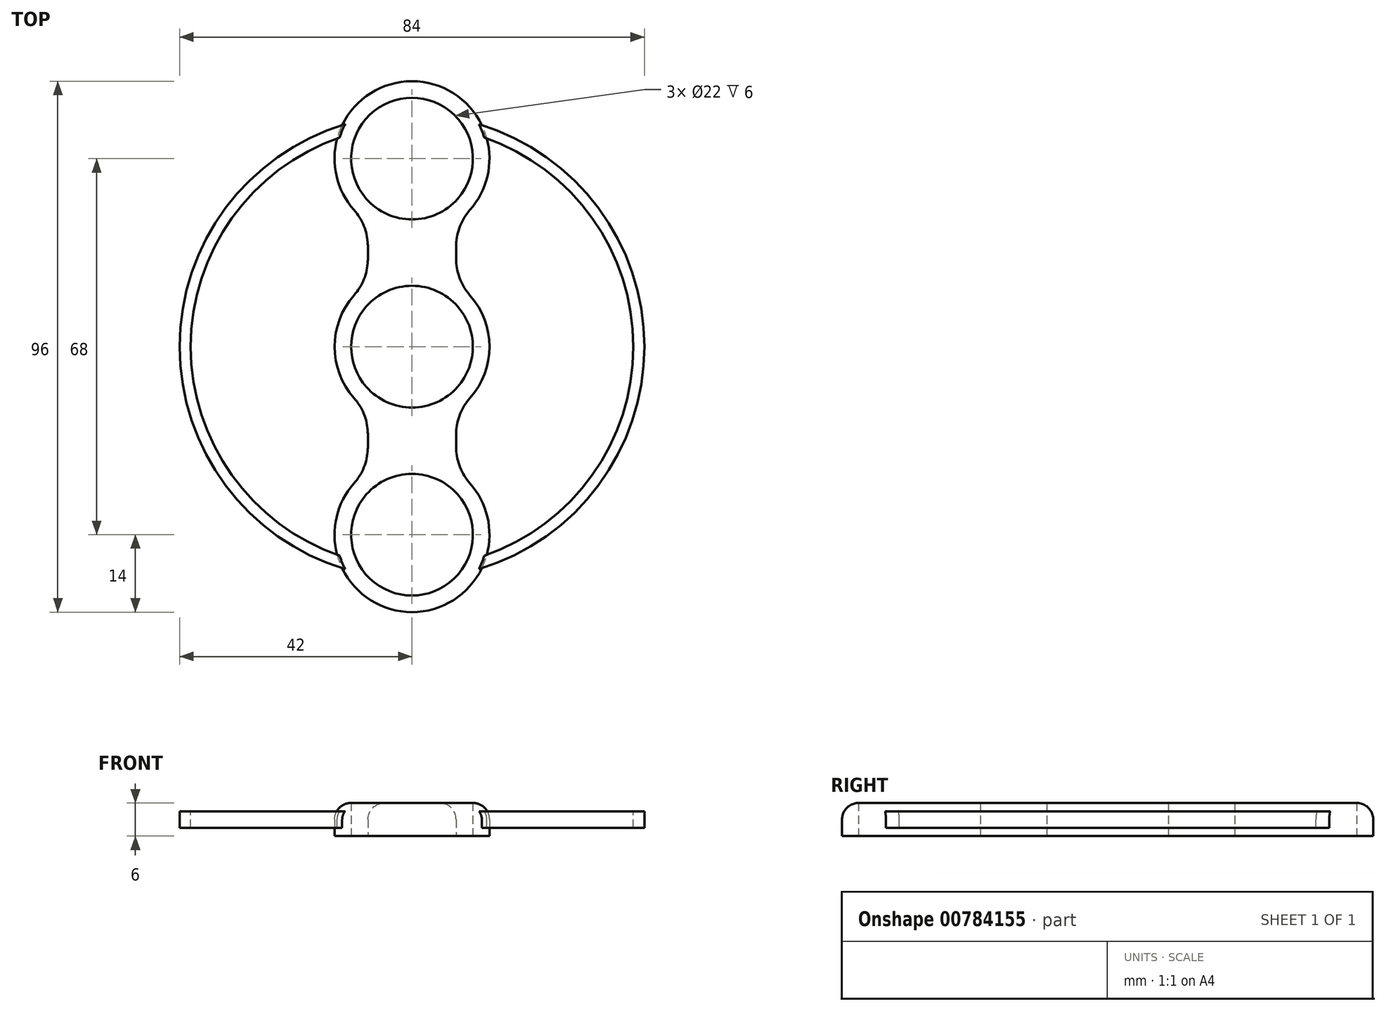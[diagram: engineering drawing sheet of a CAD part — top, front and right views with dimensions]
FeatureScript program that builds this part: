
annotation { "Feature Type Name" : "Feature", "Feature Type Description" : "" }
export const myFeature = defineFeature(function(context is Context, id is Id, definition is map)
    precondition{}
    {
        {
            var Q0;
            Q0=qCreatedBy(makeId("Top.planeOp"),FACE);
            var sketch = newSketch(context, id + "F0", { "sketchPlane" : qUnion([Q0])});
            skCircle(sketch, "E0", {"center": v(0, 0) * mm, "radius": 11 * mm});
            skCircle(sketch, "E1", {"center": v(0, 34) * mm, "radius": 11 * mm});
            skArc(sketch, "E2", {"start": v(10.49, 24.73) * mm, "mid": v(0, 48) * mm, "end": v(-10.49, 24.73) * mm});
            skArc(sketch, "E3", {"start": v(-10.49, 9.27) * mm, "mid": v(-14, 0) * mm, "end": v(-10.49, -9.27) * mm});
            skArc(sketch, "E4", {"start": v(7.99, 18.5) * mm, "mid": v(7.96, 17) * mm, "end": v(7.99, 15.5) * mm});
            skArc(sketch, "E5.MirrorC", {"start": v(-7.99, 18.5) * mm, "mid": v(-7.96, 17) * mm, "end": v(-7.99, 15.5) * mm});
            skArc(sketch, "E6.filletArc", {"start": v(10.49, 24.73) * mm, "mid": v(8.7, 21.83) * mm, "end": v(7.99, 18.5) * mm});
            skArc(sketch, "E7.filletArc", {"start": v(-7.99, 18.5) * mm, "mid": v(-8.7, 21.83) * mm, "end": v(-10.49, 24.73) * mm});
            skArc(sketch, "E8.filletArc", {"start": v(7.99, 15.5) * mm, "mid": v(8.7, 12.17) * mm, "end": v(10.49, 9.27) * mm});
            skArc(sketch, "E9.filletArc", {"start": v(-10.49, 9.27) * mm, "mid": v(-8.7, 12.17) * mm, "end": v(-7.99, 15.5) * mm});
            skArc(sketch, "E10.MirrorCS", {"start": v(-10.49, -9.27) * mm, "mid": v(-14, 0) * mm, "end": v(-10.49, 9.27) * mm});
            skArc(sketch, "E11.MirrorCS", {"start": v(7.99, -15.5) * mm, "mid": v(8.7, -12.17) * mm, "end": v(10.49, -9.27) * mm});
            skArc(sketch, "E12.MirrorCS", {"start": v(7.99, -18.5) * mm, "mid": v(7.96, -17) * mm, "end": v(7.99, -15.5) * mm});
            skArc(sketch, "E13.MirrorCS", {"start": v(10.49, -24.73) * mm, "mid": v(8.7, -21.83) * mm, "end": v(7.99, -18.5) * mm});
            skArc(sketch, "E14.MirrorCS", {"start": v(10.49, -24.73) * mm, "mid": v(0, -48) * mm, "end": v(-10.49, -24.73) * mm});
            skArc(sketch, "E15.MirrorCS", {"start": v(-7.99, -18.5) * mm, "mid": v(-8.7, -21.83) * mm, "end": v(-10.49, -24.73) * mm});
            skArc(sketch, "E16.MirrorCS", {"start": v(-7.99, -18.5) * mm, "mid": v(-7.96, -17) * mm, "end": v(-7.99, -15.5) * mm});
            skArc(sketch, "E17.MirrorCS", {"start": v(-10.49, -9.27) * mm, "mid": v(-8.7, -12.17) * mm, "end": v(-7.99, -15.5) * mm});
            skCircle(sketch, "E18.MirrorC", {"center": v(0, -34) * mm, "radius": 11 * mm});
            skArc(sketch, "E19.trimOffspring", {"start": v(10.49, 9.27) * mm, "mid": v(14, 0) * mm, "end": v(10.49, -9.27) * mm});
            skArc(sketch, "E20.trimOffspring", {"start": v(10.49, -9.27) * mm, "mid": v(14, 0) * mm, "end": v(10.49, 9.27) * mm});
            skSolve(sketch);
        }
        {
            var Q0;
            Q0 = qSketchRegion(id + "F0", true);
            var Q1;
            Q1 = qSketchRegion(id + "F2", true);
            extrude(context, id + "F1", {"entities" : qUnion([Q0, Q1]), "depth" : 1.5 * mm, "offsetDistance" : 25 * mm});
        }
        {
            var Q0;
            Q0=qCreatedBy(makeId("Top.planeOp"),FACE);
            var sketch = newSketch(context, id + "F2", { "sketchPlane" : qUnion([Q0])});
            skCircle(sketch, "E21", {"center": v(0, 0) * mm, "radius": 11 * mm});
            skCircle(sketch, "E22", {"center": v(0, 34) * mm, "radius": 11 * mm});
            skArc(sketch, "E23", {"start": v(10.49, 24.73) * mm, "mid": v(13.63, 30.8) * mm, "end": v(13.52, 37.65) * mm});
            skArc(sketch, "E24", {"start": v(-10.49, 9.27) * mm, "mid": v(-14, 0) * mm, "end": v(-10.49, -9.27) * mm});
            skArc(sketch, "E25", {"start": v(7.99, 18.5) * mm, "mid": v(7.96, 17) * mm, "end": v(7.99, 15.5) * mm});
            skArc(sketch, "E26.MirrorC", {"start": v(-7.99, 18.5) * mm, "mid": v(-7.96, 17) * mm, "end": v(-7.99, 15.5) * mm});
            skArc(sketch, "E27.filletArc", {"start": v(10.49, 24.73) * mm, "mid": v(8.7, 21.83) * mm, "end": v(7.99, 18.5) * mm});
            skArc(sketch, "E28.filletArc", {"start": v(-7.99, 18.5) * mm, "mid": v(-8.7, 21.83) * mm, "end": v(-10.49, 24.73) * mm});
            skArc(sketch, "E29.filletArc", {"start": v(-10.49, 9.27) * mm, "mid": v(-8.7, 12.17) * mm, "end": v(-7.99, 15.5) * mm});
            skArc(sketch, "E30.filletArc", {"start": v(7.99, 15.5) * mm, "mid": v(8.7, 12.17) * mm, "end": v(10.49, 9.27) * mm});
            skArc(sketch, "E31.MirrorCS", {"start": v(-10.49, -9.27) * mm, "mid": v(-13.93, 1.42) * mm, "end": v(-8.4, 11.2) * mm});
            skArc(sketch, "E32.MirrorCS", {"start": v(7.99, -15.5) * mm, "mid": v(8.7, -12.17) * mm, "end": v(10.49, -9.27) * mm});
            skArc(sketch, "E33.MirrorCS", {"start": v(7.99, -18.5) * mm, "mid": v(7.96, -17) * mm, "end": v(7.99, -15.5) * mm});
            skArc(sketch, "E34.MirrorCS", {"start": v(10.49, -24.73) * mm, "mid": v(8.7, -21.83) * mm, "end": v(7.99, -18.5) * mm});
            skArc(sketch, "E35.MirrorCS", {"start": v(10.49, -24.73) * mm, "mid": v(13.63, -30.8) * mm, "end": v(13.52, -37.65) * mm});
            skCircle(sketch, "E36.MirrorC", {"center": v(0, -34) * mm, "radius": 11 * mm});
            skArc(sketch, "E37.MirrorCS", {"start": v(-7.99, -18.5) * mm, "mid": v(-8.7, -21.83) * mm, "end": v(-10.49, -24.73) * mm});
            skArc(sketch, "E38.MirrorCS", {"start": v(-7.99, -18.5) * mm, "mid": v(-7.96, -17) * mm, "end": v(-7.99, -15.5) * mm});
            skArc(sketch, "E39.MirrorCS", {"start": v(-10.49, -9.27) * mm, "mid": v(-8.7, -12.17) * mm, "end": v(-7.99, -15.5) * mm});
            skArc(sketch, "E40.trimOffspring", {"start": v(8.4, 11.2) * mm, "mid": v(13.93, 1.42) * mm, "end": v(10.49, -9.27) * mm});
            skArc(sketch, "E41.trimOffspring", {"start": v(10.49, -9.27) * mm, "mid": v(14, 0) * mm, "end": v(10.49, 9.27) * mm});
            skArc(sketch, "E42", {"start": v(-12.62, 40.06) * mm, "mid": v(-42, 0) * mm, "end": v(-12.62, -40.06) * mm});
            skArc(sketch, "E43", {"start": v(-13.52, 37.65) * mm, "mid": v(-40, 0) * mm, "end": v(-13.52, -37.65) * mm});
            skArc(sketch, "E44.trimOffspring", {"start": v(12.62, 40.06) * mm, "mid": v(0, 48) * mm, "end": v(-12.62, 40.06) * mm});
            skArc(sketch, "E45.trimOffspring", {"start": v(-13.52, 37.65) * mm, "mid": v(-13.63, 30.8) * mm, "end": v(-10.49, 24.73) * mm});
            skArc(sketch, "E46.trimOffspring", {"start": v(13.52, -37.65) * mm, "mid": v(40, 0) * mm, "end": v(13.52, 37.65) * mm});
            skArc(sketch, "E47.trimOffspring", {"start": v(12.62, -40.06) * mm, "mid": v(0, -48) * mm, "end": v(-12.62, -40.06) * mm});
            skArc(sketch, "E48.trimOffspring", {"start": v(12.62, -40.06) * mm, "mid": v(42, 0) * mm, "end": v(12.62, 40.06) * mm});
            skArc(sketch, "E49.trimOffspring", {"start": v(-13.52, -37.65) * mm, "mid": v(-13.63, -30.8) * mm, "end": v(-10.49, -24.73) * mm});
            skSolve(sketch);
        }
        {
            var Q0;
            Q0 = qSketchRegion(id + "F2", true);
            extrude(context, id + "F3", {"entities" : qUnion([Q0]), "operationType" : NewBodyOperationType.ADD, "oppositeDirection" : true, "depth" : 3 * mm, "offsetDistance" : 25 * mm});
        }
        {
            var Q0;
            Q0=qCreatedBy(makeId("Top.planeOp"),FACE);
            cPlane(context, id + "F4", {"entities" : qUnion([Q0]), "cplaneType" : CPlaneType.OFFSET, "offset" : 1.5 * mm, "oppositeDirection" : true, "width" : 150 * mm, "height" : 150 * mm});
        }
        {
            var Q0;
            Q0=makeQuery(id+"F1.opExtrude","SWEPT_BODY",BODY,{"disambiguationData":[OSD([sQuery(id+"F0.wireOp",EDGE,"E1"),sQuery(id+"F0.wireOp",EDGE,"E2"),sQuery(id+"F0.wireOp",EDGE,"E4"),sQuery(id+"F0.wireOp",EDGE,"E5.MirrorC"),sQuery(id+"F0.wireOp",EDGE,"E6.filletArc"),sQuery(id+"F0.wireOp",EDGE,"E7.filletArc"),sQuery(id+"F0.wireOp",EDGE,"E8.filletArc"),sQuery(id+"F0.wireOp",EDGE,"E9.filletArc"),sQuery(id+"F0.wireOp",EDGE,"E10.MirrorCS"),sQuery(id+"F0.wireOp",EDGE,"E0"),sQuery(id+"F0.wireOp",EDGE,"E11.MirrorCS"),sQuery(id+"F0.wireOp",EDGE,"E12.MirrorCS"),sQuery(id+"F0.wireOp",EDGE,"E13.MirrorCS"),sQuery(id+"F0.wireOp",EDGE,"E14.MirrorCS"),sQuery(id+"F0.wireOp",EDGE,"E15.MirrorCS"),sQuery(id+"F0.wireOp",EDGE,"E16.MirrorCS"),sQuery(id+"F0.wireOp",EDGE,"E17.MirrorCS"),sQuery(id+"F0.wireOp",EDGE,"E18.MirrorC"),sQuery(id+"F0.wireOp",EDGE,"E20.trimOffspring")])]});
            var Q1;
            Q1=qCreatedBy(id+"F4.planeOp",FACE);
            mirror(context, id + "F5", {"operationType" : NewBodyOperationType.ADD, "entities" : qUnion([Q0]), "mirrorPlane" : qUnion([Q1])});
        }
        {
            var Q0;
            Q0=makeQuery(id+"F1.opExtrude","CAP_EDGE",EDGE,{"disambiguationData":[OSD([sQuery(id+"F0.wireOp",EDGE,"E2")])],"isStart":false});
            var Q1;
            Q1=makeQuery(id+"F1.opExtrude","CAP_EDGE",EDGE,{"disambiguationData":[OSD([sQuery(id+"F0.wireOp",EDGE,"E7.filletArc")])],"isStart":false});
            var Q2;
            Q2=makeQuery(id+"F1.opExtrude","CAP_EDGE",EDGE,{"disambiguationData":[OSD([sQuery(id+"F0.wireOp",EDGE,"E5.MirrorC")])],"isStart":false});
            var Q3;
            Q3=makeQuery(id+"F1.opExtrude","CAP_EDGE",EDGE,{"disambiguationData":[OSD([sQuery(id+"F0.wireOp",EDGE,"E10.MirrorCS")])],"isStart":false});
            var Q4;
            Q4=makeQuery(id+"F1.opExtrude","CAP_EDGE",EDGE,{"disambiguationData":[OSD([sQuery(id+"F0.wireOp",EDGE,"E9.filletArc")])],"isStart":false});
            var Q5;
            Q5=makeQuery(id+"F1.opExtrude","CAP_EDGE",EDGE,{"disambiguationData":[OSD([sQuery(id+"F0.wireOp",EDGE,"E17.MirrorCS")])],"isStart":false});
            var Q6;
            Q6=makeQuery(id+"F1.opExtrude","CAP_EDGE",EDGE,{"disambiguationData":[OSD([sQuery(id+"F0.wireOp",EDGE,"E16.MirrorCS")])],"isStart":false});
            var Q7;
            Q7=makeQuery(id+"F1.opExtrude","CAP_EDGE",EDGE,{"disambiguationData":[OSD([sQuery(id+"F0.wireOp",EDGE,"E14.MirrorCS")])],"isStart":false});
            var Q8;
            Q8=makeQuery(id+"F1.opExtrude","CAP_EDGE",EDGE,{"disambiguationData":[OSD([sQuery(id+"F0.wireOp",EDGE,"E13.MirrorCS")])],"isStart":false});
            var Q9;
            Q9=makeQuery(id+"F1.opExtrude","CAP_EDGE",EDGE,{"disambiguationData":[OSD([sQuery(id+"F0.wireOp",EDGE,"E15.MirrorCS")])],"isStart":false});
            var Q10;
            Q10=makeQuery(id+"F1.opExtrude","CAP_EDGE",EDGE,{"disambiguationData":[OSD([sQuery(id+"F0.wireOp",EDGE,"E12.MirrorCS")])],"isStart":false});
            var Q11;
            Q11=makeQuery(id+"F1.opExtrude","CAP_EDGE",EDGE,{"disambiguationData":[OSD([sQuery(id+"F0.wireOp",EDGE,"E11.MirrorCS")])],"isStart":false});
            var Q12;
            Q12=makeQuery(id+"F1.opExtrude","CAP_EDGE",EDGE,{"disambiguationData":[OSD([sQuery(id+"F0.wireOp",EDGE,"E20.trimOffspring")])],"isStart":false});
            var Q13;
            Q13=makeQuery(id+"F1.opExtrude","CAP_EDGE",EDGE,{"disambiguationData":[OSD([sQuery(id+"F0.wireOp",EDGE,"E8.filletArc")])],"isStart":false});
            var Q14;
            Q14=makeQuery(id+"F1.opExtrude","CAP_EDGE",EDGE,{"disambiguationData":[OSD([sQuery(id+"F0.wireOp",EDGE,"E4")])],"isStart":false});
            var Q15;
            Q15=makeQuery(id+"F5.opPattern","COPY",EDGE,{"derivedFrom":makeQuery(id+"F1.opExtrude","CAP_EDGE",EDGE,{"disambiguationData":[OSD([sQuery(id+"F0.wireOp",EDGE,"E20.trimOffspring")])],"isStart":false}),"instanceName":"1"});
            fillet(context, id + "F6", {"entities" : qUnion([Q0, Q1, Q2, Q3, Q4, Q5, Q6, Q7, Q8, Q9, Q10, Q11, Q12, Q13, Q14, Q15]), "radius" : 3 * mm, "tangentPropagation" : true, "allowEdgeOverflow" : false});
        }
    });
